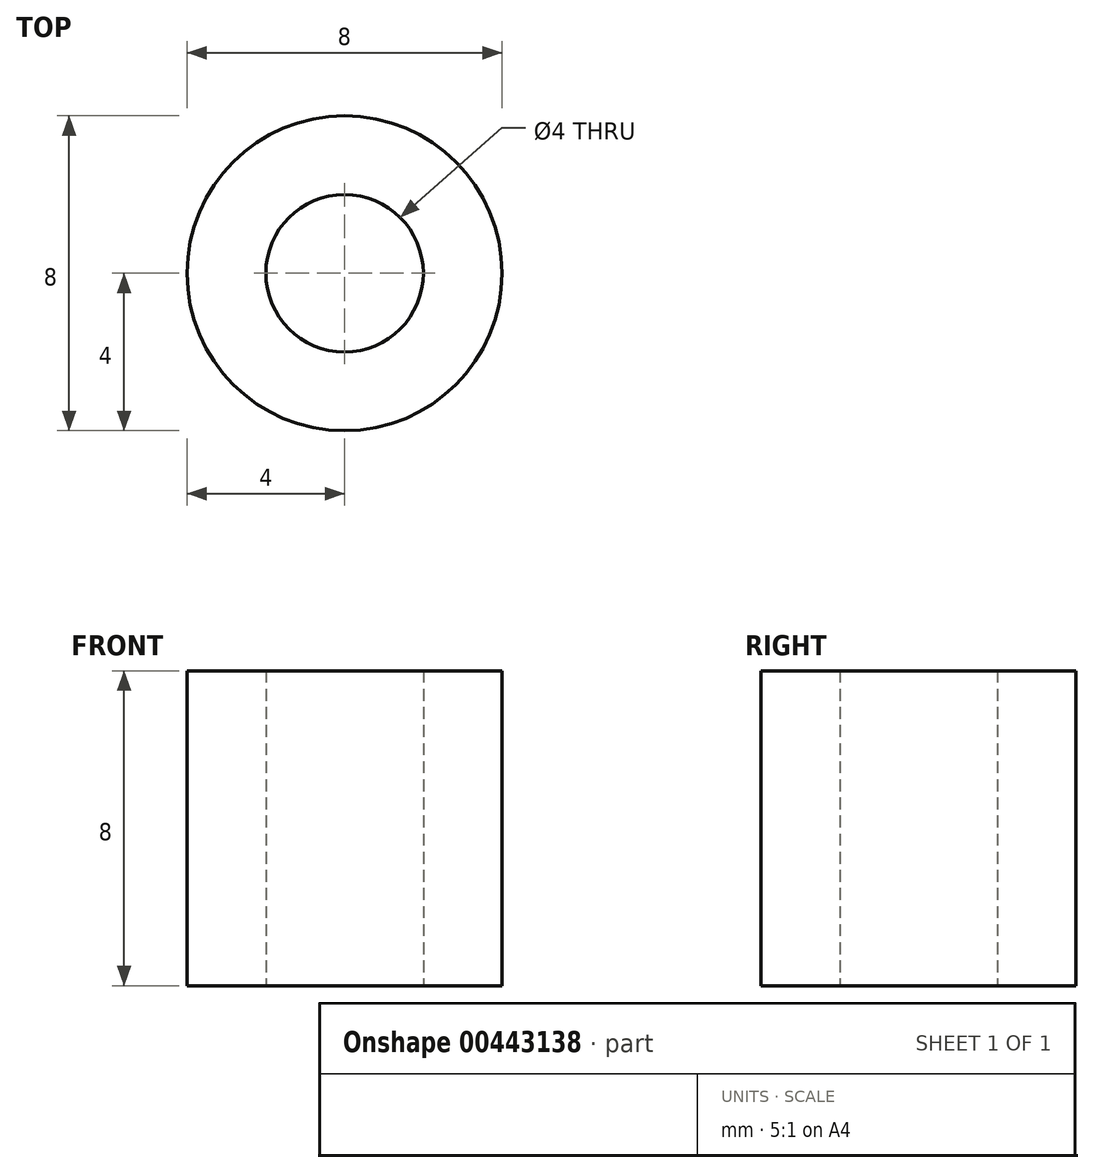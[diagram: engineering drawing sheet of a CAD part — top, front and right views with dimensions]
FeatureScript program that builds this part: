
annotation { "Feature Type Name" : "Feature", "Feature Type Description" : "" }
export const myFeature = defineFeature(function(context is Context, id is Id, definition is map)
    precondition{}
    {
        {
            var Q0;
            Q0=qCreatedBy(makeId("Top.planeOp"),FACE);
            var sketch = newSketch(context, id + "F0", { "sketchPlane" : qUnion([Q0])});
            skCircle(sketch, "E0", {"center": v(0, 0) * mm, "radius": 2 * mm});
            skCircle(sketch, "E1", {"center": v(0, 0) * mm, "radius": 4 * mm});
            skSolve(sketch);
        }
        {
            var Q0;
            Q0=makeQuery(id+"F0.imprint","IMPRINT",FACE,{"disambiguationData":[TD([[makeQuery(id+"F0.imprint","IMPRINT",EDGE,{"derivedFrom":sQuery(id+"F0.wireOp",EDGE,"E0")}),-1.0]])]});
            extrude(context, id + "F1", {"entities" : qUnion([Q0]), "offsetDistance" : 25 * mm, "depth" : 8 * mm});
        }
    });
